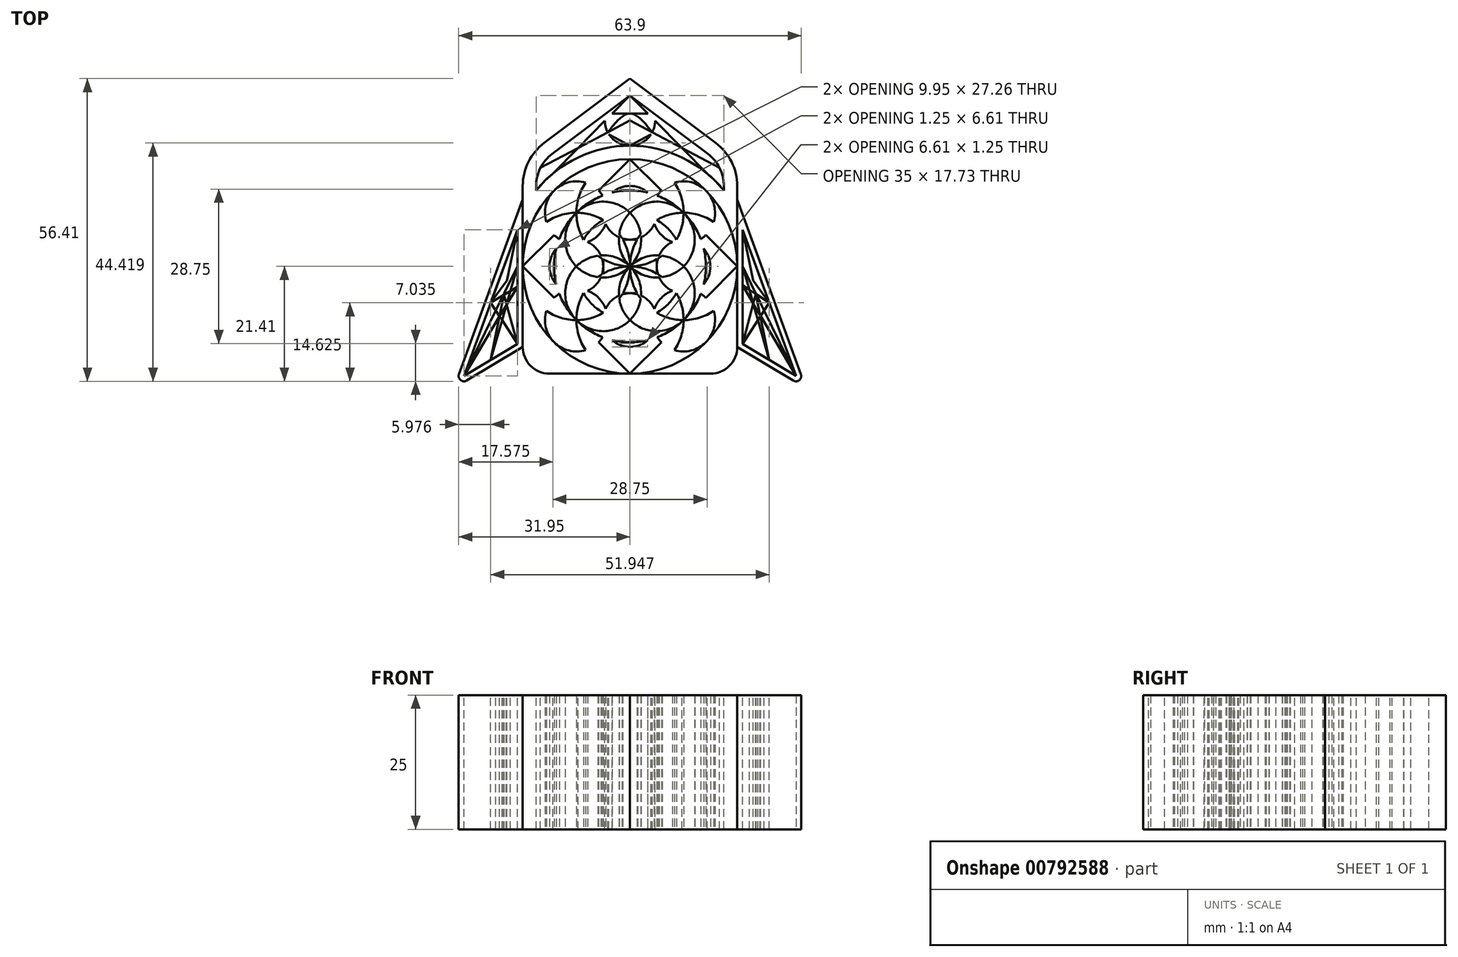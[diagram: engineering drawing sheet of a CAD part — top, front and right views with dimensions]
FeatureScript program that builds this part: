
annotation { "Feature Type Name" : "Feature", "Feature Type Description" : "" }
export const myFeature = defineFeature(function(context is Context, id is Id, definition is map)
    precondition{}
    {
        {
            var Q0;
            Q0=qCreatedBy(makeId("Top.planeOp"),FACE);
            var sketch = newSketch(context, id + "F0", { "sketchPlane" : qUnion([Q0])});
            skLineSegment(sketch, "E0.bottom", {"start": v(-20, 20) * mm, "end": v(20, 20) * mm});
            skLineSegment(sketch, "E0.top", {"start": v(-20, -20) * mm, "end": v(20, -20) * mm});
            skLineSegment(sketch, "E0.left", {"start": v(-20, 20) * mm, "end": v(-20, -20) * mm});
            skLineSegment(sketch, "E0.right", {"start": v(20, 20) * mm, "end": v(20, -20) * mm});
            skPoint(sketch, "E0.middle", {"position": v(0, 0) * mm});
            skCircle(sketch, "E1", {"center": v(0, 0) * mm, "radius": 20 * mm});
            skLineSegment(sketch, "E2", {"start": v(20, 20) * mm, "end": v(-20, -20) * mm, "construction": true});
            skLineSegment(sketch, "E3", {"start": v(-20, 20) * mm, "end": v(0, 35) * mm});
            skLineSegment(sketch, "E4", {"start": v(0, 35) * mm, "end": v(20, 20) * mm});
            skLineSegment(sketch, "E5", {"start": v(0, 35) * mm, "end": v(0, -20) * mm, "construction": true});
            skLineSegment(sketch, "E6", {"start": v(-20, 20) * mm, "end": v(20, -20) * mm, "construction": true});
            skLineSegment(sketch, "E7", {"start": v(0, 20) * mm, "end": v(-10, 20) * mm});
            skLineSegment(sketch, "E8", {"start": v(0, 20) * mm, "end": v(10, 20) * mm});
            skLineSegment(sketch, "E9", {"start": v(20, 20) * mm, "end": v(20, 12.5) * mm});
            skLineSegment(sketch, "E10", {"start": v(20, 12.5) * mm, "end": v(32.86, -22.73) * mm});
            skLineSegment(sketch, "E11", {"start": v(32.86, -22.73) * mm, "end": v(20, -15) * mm});
            skLineSegment(sketch, "E12", {"start": v(20, -15) * mm, "end": v(20, -20) * mm});
            skLineSegment(sketch, "E13", {"start": v(-20, 20) * mm, "end": v(-20, 12.5) * mm});
            skLineSegment(sketch, "E14", {"start": v(-20, 12.5) * mm, "end": v(-32.86, -22.73) * mm});
            skLineSegment(sketch, "E15", {"start": v(-32.86, -22.73) * mm, "end": v(-20, -15) * mm});
            skLineSegment(sketch, "E16", {"start": v(-20, -15) * mm, "end": v(-20, -20) * mm});
            skSolve(sketch);
        }
        {
            var Q0;
            {var subQ3=sQuery(id+"F0.wireOp",EDGE,"E3");Q0=makeQuery(id+"F0.imprint","IMPRINT",FACE,{"disambiguationData":[TD([[makeQuery(id+"F0.imprint","IMPRINT",EDGE,{"derivedFrom":subQ3}),-1.0]])]});}
            var Q1;
            {var subQ3=sQuery(id+"F0.wireOp",EDGE,"E3");Q1=makeQuery(id+"F0.imprint","IMPRINT",FACE,{"disambiguationData":[TD([[makeQuery(id+"F0.imprint","IMPRINT",EDGE,{"derivedFrom":subQ3}),-1.0]])]});}
            var Q2;
            {var subQ3=sQuery(id+"F0.wireOp",EDGE,"0a9cf247-4ca8-4cc3-be67-cc762b10b733");Q2=makeQuery(id+"F0.imprint","IMPRINT",FACE,{"disambiguationData":[TD([[makeQuery(id+"F0.imprint","IMPRINT",EDGE,{"derivedFrom":subQ3}),-1.0]])]});}
            var Q3;
            {var subQ1=sQuery(id+"F0.wireOp",EDGE,"E0.bottom");var subQ6=makeQuery(id+"F0.imprint","IMPRINT",VERTEX,{"disambiguationData":[OD(1.0)],"derivedFrom":subQ1});Q3=makeQuery(id+"F0.imprint","IMPRINT",FACE,{"disambiguationData":[TD([[makeQuery(id+"F0.imprint","IMPRINT",EDGE,{"disambiguationData":[TD([[subQ6,-1.0]])],"derivedFrom":subQ1}),-1.0]])]});}
            var Q4;
            {var subQ1=sQuery(id+"F0.wireOp",EDGE,"E0.bottom");var subQ6=makeQuery(id+"F0.imprint","IMPRINT",VERTEX,{"disambiguationData":[OD(0.0)],"derivedFrom":subQ1});Q4=makeQuery(id+"F0.imprint","IMPRINT",FACE,{"disambiguationData":[TD([[makeQuery(id+"F0.imprint","IMPRINT",EDGE,{"disambiguationData":[TD([[subQ6,1.0]])],"derivedFrom":subQ1}),-1.0]])]});}
            var Q5;
            {var subQ0=sQuery(id+"F0.wireOp",EDGE,"E0.right");var subQ1=sQuery(id+"F0.wireOp",EDGE,"E0.top");var subQ2=makeQuery(id+"F0.imprint","INTERSECT",VERTEX,{"derivedFrom":[subQ1,subQ0]});var subQ7=sQuery(id+"F0.wireOp",EDGE,"E0.left");var subQ8=makeQuery(id+"F0.imprint","INTERSECT",VERTEX,{"derivedFrom":[subQ1,subQ7]});Q5=qUnion([makeQuery(id+"F0.imprint","IMPRINT",FACE,{"disambiguationData":[TD([[makeQuery(id+"F0.imprint","IMPRINT",EDGE,{"disambiguationData":[TD([[subQ8,-1.0]])],"derivedFrom":subQ1}),1.0]])]}),makeQuery(id+"F0.imprint","IMPRINT",FACE,{"disambiguationData":[TD([[makeQuery(id+"F0.imprint","IMPRINT",EDGE,{"disambiguationData":[TD([[subQ2,1.0]])],"derivedFrom":subQ1}),1.0]])]})]);}
            var Q6;
            {var subQ0=sQuery(id+"F0.wireOp",EDGE,"E0.right");var subQ1=sQuery(id+"F0.wireOp",EDGE,"E0.top");var subQ2=makeQuery(id+"F0.imprint","INTERSECT",VERTEX,{"derivedFrom":[subQ1,subQ0]});var subQ7=sQuery(id+"F0.wireOp",EDGE,"E0.left");var subQ8=makeQuery(id+"F0.imprint","INTERSECT",VERTEX,{"derivedFrom":[subQ1,subQ7]});Q6=qUnion([makeQuery(id+"F0.imprint","IMPRINT",FACE,{"disambiguationData":[TD([[makeQuery(id+"F0.imprint","IMPRINT",EDGE,{"disambiguationData":[TD([[subQ8,-1.0]])],"derivedFrom":subQ1}),1.0]])]}),makeQuery(id+"F0.imprint","IMPRINT",FACE,{"disambiguationData":[TD([[makeQuery(id+"F0.imprint","IMPRINT",EDGE,{"disambiguationData":[TD([[subQ2,1.0]])],"derivedFrom":subQ1}),1.0]])]})]);}
            var Q7;
            {var subQ0=sQuery(id+"F0.wireOp",EDGE,"Tc6ELDUx-aZw6-dxSL-uZ0s-LFfPMrrENeSc");Q7=makeQuery(id+"F0.imprint","IMPRINT",FACE,{"disambiguationData":[TD([[makeQuery(id+"F0.imprint","IMPRINT",EDGE,{"derivedFrom":subQ0}),-1.0]])]});}
            var Q8;
            {var subQ0=sQuery(id+"F0.wireOp",EDGE,"qauVQVhD-89ha-aMvt-0F9t-eZ8ksP4P0BOe");Q8=makeQuery(id+"F0.imprint","IMPRINT",FACE,{"disambiguationData":[TD([[makeQuery(id+"F0.imprint","IMPRINT",EDGE,{"derivedFrom":subQ0}),-1.0]])]});}
            var Q9;
            {var subQ3=sQuery(id+"F0.wireOp",EDGE,"E3");Q9=makeQuery(id+"F0.imprint","IMPRINT",FACE,{"disambiguationData":[TD([[makeQuery(id+"F0.imprint","IMPRINT",EDGE,{"derivedFrom":subQ3}),-1.0]])]});}
            extrude(context, id + "F1", {"entities" : qUnion([Q0, Q1, Q2, Q3, Q4, Q5, Q6, Q7, Q8, Q9]), "endBound" : BoundingType.SYMMETRIC, "depth" : 25 * mm, "offsetDistance" : 25 * mm});
        }
        {
            var Q0;
            Q0=makeQuery(id+"F1.opExtrude","SWEPT_EDGE",EDGE,{"disambiguationData":[OSD([sQuery(id+"F0.wireOp",EDGE,"E0.bottom"),sQuery(id+"F0.wireOp",EDGE,"E0.left"),sQuery(id+"F0.wireOp",EDGE,"E3")])]});
            var Q1;
            Q1=makeQuery(id+"F1.opExtrude","SWEPT_EDGE",EDGE,{"disambiguationData":[OSD([sQuery(id+"F0.wireOp",EDGE,"E0.bottom"),sQuery(id+"F0.wireOp",EDGE,"E0.right"),sQuery(id+"F0.wireOp",EDGE,"E4")])]});
            fillet(context, id + "F2", {"entities" : qUnion([Q0, Q1]), "radius" : 10 * mm, "tangentPropagation" : true, "allowEdgeOverflow" : false});
        }
        {
            var Q0;
            Q0=makeQuery(id+"F1.opExtrude","CAP_FACE",FACE,{"disambiguationData":[OSD([sQuery(id+"F0.wireOp",EDGE,"E0.left"),sQuery(id+"F0.wireOp",EDGE,"E0.right"),sQuery(id+"F0.wireOp",EDGE,"E1"),sQuery(id+"F0.wireOp",EDGE,"E3"),sQuery(id+"F0.wireOp",EDGE,"E4")])],"isStart":false});
            var Q1;
            Q1=makeQuery(id+"F1.opExtrude","CAP_FACE",FACE,{"disambiguationData":[OSD([sQuery(id+"F0.wireOp",EDGE,"E0.left"),sQuery(id+"F0.wireOp",EDGE,"E0.right"),sQuery(id+"F0.wireOp",EDGE,"E1"),sQuery(id+"F0.wireOp",EDGE,"E3"),sQuery(id+"F0.wireOp",EDGE,"E4")])],"isStart":true});
            shell(context, id + "F3", {"entities" : qUnion([Q0, Q1]), "thickness" : 2.5 * mm});
        }
        {
            var Q0;
            Q0=qCreatedBy(makeId("Top.planeOp"),FACE);
            var sketch = newSketch(context, id + "F4", { "sketchPlane" : qUnion([Q0])});
            skCircle(sketch, "E17", {"center": v(0, 0) * mm, "radius": 20 * mm});
            skLineSegment(sketch, "E18", {"start": v(0, 0) * mm, "end": v(0, 20) * mm});
            skLineSegment(sketch, "E19", {"start": v(0, 0) * mm, "end": v(0, -20) * mm});
            skLineSegment(sketch, "E20", {"start": v(0, 0) * mm, "end": v(20, 0) * mm});
            skLineSegment(sketch, "E21", {"start": v(0, 0) * mm, "end": v(-20, 0) * mm});
            skLineSegment(sketch, "E22", {"start": v(0, 20) * mm, "end": v(-20, 0) * mm});
            skLineSegment(sketch, "E23", {"start": v(-20, 0) * mm, "end": v(0, -20) * mm});
            skLineSegment(sketch, "E24", {"start": v(0, -20) * mm, "end": v(20, 0) * mm});
            skLineSegment(sketch, "E25", {"start": v(20, 0) * mm, "end": v(0, 20) * mm});
            skLineSegment(sketch, "E26", {"start": v(0, 0) * mm, "end": v(-10, 10) * mm});
            skLineSegment(sketch, "E27", {"start": v(0, 0) * mm, "end": v(10, -10) * mm});
            skLineSegment(sketch, "E28", {"start": v(0, 0) * mm, "end": v(10, 10) * mm});
            skLineSegment(sketch, "E29", {"start": v(0, 0) * mm, "end": v(-10, -10) * mm});
            skCircle(sketch, "E30", {"center": v(-5, 5) * mm, "radius": 7.07 * mm});
            skCircle(sketch, "E31", {"center": v(5, 5) * mm, "radius": 7.07 * mm});
            skCircle(sketch, "E32", {"center": v(5, -5) * mm, "radius": 7.07 * mm});
            skCircle(sketch, "E33", {"center": v(-5, -5) * mm, "radius": 7.07 * mm});
            skCircle(sketch, "E34", {"center": v(0, -10) * mm, "radius": 10 * mm});
            skCircle(sketch, "E35", {"center": v(10, 0) * mm, "radius": 10 * mm});
            skCircle(sketch, "E36", {"center": v(0, 10) * mm, "radius": 10 * mm});
            skCircle(sketch, "E37", {"center": v(-10, 0) * mm, "radius": 10 * mm});
            skLineSegment(sketch, "E38", {"start": v(5, 5) * mm, "end": v(5, -5) * mm});
            skLineSegment(sketch, "E39", {"start": v(-5, -5) * mm, "end": v(5, -5) * mm});
            skLineSegment(sketch, "E40", {"start": v(-5, -5) * mm, "end": v(-5, 5) * mm});
            skLineSegment(sketch, "E41", {"start": v(-5, 5) * mm, "end": v(5, 5) * mm});
            skLineSegment(sketch, "E42", {"start": v(-10, 10) * mm, "end": v(10, 10) * mm});
            skLineSegment(sketch, "E43", {"start": v(10, 10) * mm, "end": v(10, -10) * mm});
            skLineSegment(sketch, "E44", {"start": v(10, -10) * mm, "end": v(-10, -10) * mm});
            skLineSegment(sketch, "E45", {"start": v(-10, -10) * mm, "end": v(-10, 10) * mm});
            skCircle(sketch, "E46", {"center": v(-10, -10) * mm, "radius": 5.86 * mm});
            skCircle(sketch, "E47", {"center": v(10, -10) * mm, "radius": 5.86 * mm});
            skCircle(sketch, "E48", {"center": v(10, 10) * mm, "radius": 5.86 * mm});
            skCircle(sketch, "E49", {"center": v(-10, 10) * mm, "radius": 5.86 * mm});
            skCircle(sketch, "E50", {"center": v(0, 0) * mm, "radius": 10 * mm});
            skCircle(sketch, "E51", {"center": v(0, 0) * mm, "radius": 14.14 * mm});
            skCircle(sketch, "E52", {"center": v(10, 0) * mm, "radius": 5 * mm});
            skCircle(sketch, "E53", {"center": v(0, -10) * mm, "radius": 5 * mm});
            skCircle(sketch, "E54", {"center": v(-10, 0) * mm, "radius": 5 * mm});
            skCircle(sketch, "E55", {"center": v(0, 10) * mm, "radius": 5 * mm});
            skSolve(sketch);
        }
        {
            var Q0;
            {var subQ0=sQuery(id+"F4.wireOp",EDGE,"E37");var subQ3=sQuery(id+"F4.wireOp",EDGE,"E41");var subQ5=makeQuery(id+"F4.imprint","INTERSECT",VERTEX,{"derivedFrom":[subQ0,subQ3]});Q0=makeQuery(id+"F4.imprint","IMPRINT",FACE,{"disambiguationData":[TD([[makeQuery(id+"F4.imprint","IMPRINT",EDGE,{"disambiguationData":[TD([[subQ5,-1.0]])],"derivedFrom":subQ3}),-1.0]])]});}
            var Q1;
            {var subQ0=sQuery(id+"F4.wireOp",EDGE,"E35");var subQ3=sQuery(id+"F4.wireOp",EDGE,"E41");var subQ5=makeQuery(id+"F4.imprint","INTERSECT",VERTEX,{"derivedFrom":[subQ0,subQ3]});Q1=makeQuery(id+"F4.imprint","IMPRINT",FACE,{"disambiguationData":[TD([[makeQuery(id+"F4.imprint","IMPRINT",EDGE,{"disambiguationData":[TD([[subQ5,1.0]])],"derivedFrom":subQ3}),-1.0]])]});}
            var Q2;
            {var subQ0=sQuery(id+"F4.wireOp",EDGE,"E36");var subQ3=sQuery(id+"F4.wireOp",EDGE,"E38");var subQ5=makeQuery(id+"F4.imprint","INTERSECT",VERTEX,{"derivedFrom":[subQ0,subQ3]});Q2=makeQuery(id+"F4.imprint","IMPRINT",FACE,{"disambiguationData":[TD([[makeQuery(id+"F4.imprint","IMPRINT",EDGE,{"disambiguationData":[TD([[subQ5,-1.0]])],"derivedFrom":subQ3}),-1.0]])]});}
            var Q3;
            {var subQ0=sQuery(id+"F4.wireOp",EDGE,"E34");var subQ3=sQuery(id+"F4.wireOp",EDGE,"E38");var subQ5=makeQuery(id+"F4.imprint","INTERSECT",VERTEX,{"derivedFrom":[subQ0,subQ3]});Q3=makeQuery(id+"F4.imprint","IMPRINT",FACE,{"disambiguationData":[TD([[makeQuery(id+"F4.imprint","IMPRINT",EDGE,{"disambiguationData":[TD([[subQ5,1.0]])],"derivedFrom":subQ3}),-1.0]])]});}
            var Q4;
            {var subQ0=sQuery(id+"F4.wireOp",EDGE,"E35");var subQ3=sQuery(id+"F4.wireOp",EDGE,"E39");var subQ5=makeQuery(id+"F4.imprint","INTERSECT",VERTEX,{"derivedFrom":[subQ0,subQ3]});Q4=makeQuery(id+"F4.imprint","IMPRINT",FACE,{"disambiguationData":[TD([[makeQuery(id+"F4.imprint","IMPRINT",EDGE,{"disambiguationData":[TD([[subQ5,1.0]])],"derivedFrom":subQ3}),1.0]])]});}
            var Q5;
            {var subQ0=sQuery(id+"F4.wireOp",EDGE,"E37");var subQ3=sQuery(id+"F4.wireOp",EDGE,"E39");var subQ5=makeQuery(id+"F4.imprint","INTERSECT",VERTEX,{"derivedFrom":[subQ0,subQ3]});Q5=makeQuery(id+"F4.imprint","IMPRINT",FACE,{"disambiguationData":[TD([[makeQuery(id+"F4.imprint","IMPRINT",EDGE,{"disambiguationData":[TD([[subQ5,-1.0]])],"derivedFrom":subQ3}),1.0]])]});}
            var Q6;
            {var subQ0=sQuery(id+"F4.wireOp",EDGE,"E34");var subQ3=sQuery(id+"F4.wireOp",EDGE,"E40");var subQ5=makeQuery(id+"F4.imprint","INTERSECT",VERTEX,{"derivedFrom":[subQ0,subQ3]});Q6=makeQuery(id+"F4.imprint","IMPRINT",FACE,{"disambiguationData":[TD([[makeQuery(id+"F4.imprint","IMPRINT",EDGE,{"disambiguationData":[TD([[subQ5,-1.0]])],"derivedFrom":subQ3}),-1.0]])]});}
            var Q7;
            {var subQ0=sQuery(id+"F4.wireOp",EDGE,"E36");var subQ3=sQuery(id+"F4.wireOp",EDGE,"E40");var subQ5=makeQuery(id+"F4.imprint","INTERSECT",VERTEX,{"derivedFrom":[subQ0,subQ3]});Q7=makeQuery(id+"F4.imprint","IMPRINT",FACE,{"disambiguationData":[TD([[makeQuery(id+"F4.imprint","IMPRINT",EDGE,{"disambiguationData":[TD([[subQ5,1.0]])],"derivedFrom":subQ3}),-1.0]])]});}
            var Q8;
            {var subQ3=sQuery(id+"F4.wireOp",EDGE,"E33");var subQ5=sQuery(id+"F4.wireOp",EDGE,"E36");var subQ6=makeQuery(id+"F4.imprint","INTERSECT",VERTEX,{"derivedFrom":[subQ3,subQ5]});Q8=makeQuery(id+"F4.imprint","IMPRINT",FACE,{"disambiguationData":[TD([[makeQuery(id+"F4.imprint","IMPRINT",EDGE,{"disambiguationData":[TD([[subQ6,-1.0]])],"derivedFrom":subQ5}),-1.0]])]});}
            var Q9;
            {var subQ3=sQuery(id+"F4.wireOp",EDGE,"E30");var subQ5=sQuery(id+"F4.wireOp",EDGE,"E34");var subQ6=makeQuery(id+"F4.imprint","INTERSECT",VERTEX,{"derivedFrom":[subQ3,subQ5]});Q9=makeQuery(id+"F4.imprint","IMPRINT",FACE,{"disambiguationData":[TD([[makeQuery(id+"F4.imprint","IMPRINT",EDGE,{"disambiguationData":[TD([[subQ6,1.0]])],"derivedFrom":subQ5}),-1.0]])]});}
            var Q10;
            {var subQ3=sQuery(id+"F4.wireOp",EDGE,"E32");var subQ5=sQuery(id+"F4.wireOp",EDGE,"E37");var subQ6=makeQuery(id+"F4.imprint","INTERSECT",VERTEX,{"derivedFrom":[subQ3,subQ5]});Q10=makeQuery(id+"F4.imprint","IMPRINT",FACE,{"disambiguationData":[TD([[makeQuery(id+"F4.imprint","IMPRINT",EDGE,{"disambiguationData":[TD([[subQ6,-1.0]])],"derivedFrom":subQ5}),-1.0]])]});}
            var Q11;
            {var subQ3=sQuery(id+"F4.wireOp",EDGE,"E33");var subQ5=sQuery(id+"F4.wireOp",EDGE,"E35");var subQ6=makeQuery(id+"F4.imprint","INTERSECT",VERTEX,{"derivedFrom":[subQ3,subQ5]});Q11=makeQuery(id+"F4.imprint","IMPRINT",FACE,{"disambiguationData":[TD([[makeQuery(id+"F4.imprint","IMPRINT",EDGE,{"disambiguationData":[TD([[subQ6,1.0]])],"derivedFrom":subQ5}),-1.0]])]});}
            var Q12;
            {var subQ3=sQuery(id+"F4.wireOp",EDGE,"E31");var subQ5=sQuery(id+"F4.wireOp",EDGE,"E34");var subQ6=makeQuery(id+"F4.imprint","INTERSECT",VERTEX,{"derivedFrom":[subQ3,subQ5]});Q12=makeQuery(id+"F4.imprint","IMPRINT",FACE,{"disambiguationData":[TD([[makeQuery(id+"F4.imprint","IMPRINT",EDGE,{"disambiguationData":[TD([[subQ6,-1.0]])],"derivedFrom":subQ5}),-1.0]])]});}
            var Q13;
            {var subQ3=sQuery(id+"F4.wireOp",EDGE,"E32");var subQ5=sQuery(id+"F4.wireOp",EDGE,"E36");var subQ6=makeQuery(id+"F4.imprint","INTERSECT",VERTEX,{"derivedFrom":[subQ3,subQ5]});Q13=makeQuery(id+"F4.imprint","IMPRINT",FACE,{"disambiguationData":[TD([[makeQuery(id+"F4.imprint","IMPRINT",EDGE,{"disambiguationData":[TD([[subQ6,1.0]])],"derivedFrom":subQ5}),-1.0]])]});}
            var Q14;
            {var subQ3=sQuery(id+"F4.wireOp",EDGE,"E31");var subQ5=sQuery(id+"F4.wireOp",EDGE,"E37");var subQ6=makeQuery(id+"F4.imprint","INTERSECT",VERTEX,{"derivedFrom":[subQ3,subQ5]});Q14=makeQuery(id+"F4.imprint","IMPRINT",FACE,{"disambiguationData":[TD([[makeQuery(id+"F4.imprint","IMPRINT",EDGE,{"disambiguationData":[TD([[subQ6,1.0]])],"derivedFrom":subQ5}),-1.0]])]});}
            var Q15;
            {var subQ3=sQuery(id+"F4.wireOp",EDGE,"E30");var subQ5=sQuery(id+"F4.wireOp",EDGE,"E35");var subQ6=makeQuery(id+"F4.imprint","INTERSECT",VERTEX,{"derivedFrom":[subQ3,subQ5]});Q15=makeQuery(id+"F4.imprint","IMPRINT",FACE,{"disambiguationData":[TD([[makeQuery(id+"F4.imprint","IMPRINT",EDGE,{"disambiguationData":[TD([[subQ6,-1.0]])],"derivedFrom":subQ5}),-1.0]])]});}
            var Q16;
            {var subQ0=sQuery(id+"F4.wireOp",EDGE,"E46");var subQ1=sQuery(id+"F4.wireOp",EDGE,"E33");var subQ2=makeQuery(id+"F4.imprint","INTERSECT",VERTEX,{"disambiguationData":[OD(0.0)],"derivedFrom":[subQ1,subQ0]});Q16=makeQuery(id+"F4.imprint","IMPRINT",FACE,{"disambiguationData":[TD([[makeQuery(id+"F4.imprint","IMPRINT",EDGE,{"disambiguationData":[TD([[subQ2,-1.0]])],"derivedFrom":subQ0}),-1.0]])]});}
            var Q17;
            {var subQ5=sQuery(id+"F4.wireOp",EDGE,"E49");var subQ6=sQuery(id+"F4.wireOp",EDGE,"E30");var subQ7=makeQuery(id+"F4.imprint","INTERSECT",VERTEX,{"disambiguationData":[OD(1.0)],"derivedFrom":[subQ6,subQ5]});Q17=makeQuery(id+"F4.imprint","IMPRINT",FACE,{"disambiguationData":[TD([[makeQuery(id+"F4.imprint","IMPRINT",EDGE,{"disambiguationData":[TD([[subQ7,1.0]])],"derivedFrom":subQ5}),-1.0]])]});}
            var Q18;
            {var subQ0=sQuery(id+"F4.wireOp",EDGE,"E51");var subQ1=sQuery(id+"F4.wireOp",EDGE,"E49");var subQ2=makeQuery(id+"F4.imprint","INTERSECT",VERTEX,{"disambiguationData":[OD(1.0)],"derivedFrom":[subQ1,subQ0]});Q18=makeQuery(id+"F4.imprint","IMPRINT",FACE,{"disambiguationData":[TD([[makeQuery(id+"F4.imprint","IMPRINT",EDGE,{"disambiguationData":[TD([[subQ2,-1.0]])],"derivedFrom":subQ1}),-1.0]])]});}
            var Q19;
            {var subQ0=sQuery(id+"F4.wireOp",EDGE,"E51");var subQ5=sQuery(id+"F4.wireOp",EDGE,"E49");var subQ6=makeQuery(id+"F4.imprint","INTERSECT",VERTEX,{"disambiguationData":[OD(1.0)],"derivedFrom":[subQ5,subQ0]});Q19=makeQuery(id+"F4.imprint","IMPRINT",FACE,{"disambiguationData":[TD([[makeQuery(id+"F4.imprint","IMPRINT",EDGE,{"disambiguationData":[TD([[subQ6,-1.0]])],"derivedFrom":subQ5}),1.0]])]});}
            var Q20;
            {var subQ0=sQuery(id+"F4.wireOp",EDGE,"E54");var subQ1=sQuery(id+"F4.wireOp",EDGE,"E46");var subQ2=makeQuery(id+"F4.imprint","INTERSECT",VERTEX,{"disambiguationData":[OD(1.0)],"derivedFrom":[subQ1,subQ0]});Q20=makeQuery(id+"F4.imprint","IMPRINT",FACE,{"disambiguationData":[TD([[makeQuery(id+"F4.imprint","IMPRINT",EDGE,{"disambiguationData":[TD([[subQ2,-1.0]])],"derivedFrom":subQ1}),-1.0]])]});}
            var Q21;
            {var subQ3=sQuery(id+"F4.wireOp",EDGE,"E54");var subQ5=sQuery(id+"F4.wireOp",EDGE,"E46");var subQ6=makeQuery(id+"F4.imprint","INTERSECT",VERTEX,{"disambiguationData":[OD(1.0)],"derivedFrom":[subQ5,subQ3]});Q21=makeQuery(id+"F4.imprint","IMPRINT",FACE,{"disambiguationData":[TD([[makeQuery(id+"F4.imprint","IMPRINT",EDGE,{"disambiguationData":[TD([[subQ6,-1.0]])],"derivedFrom":subQ5}),1.0]])]});}
            var Q22;
            {var subQ0=sQuery(id+"F4.wireOp",EDGE,"E46");var subQ1=sQuery(id+"F4.wireOp",EDGE,"E33");var subQ2=makeQuery(id+"F4.imprint","INTERSECT",VERTEX,{"disambiguationData":[OD(1.0)],"derivedFrom":[subQ1,subQ0]});Q22=makeQuery(id+"F4.imprint","IMPRINT",FACE,{"disambiguationData":[TD([[makeQuery(id+"F4.imprint","IMPRINT",EDGE,{"disambiguationData":[TD([[subQ2,1.0]])],"derivedFrom":subQ0}),-1.0]])]});}
            var Q23;
            {var subQ5=sQuery(id+"F4.wireOp",EDGE,"E47");var subQ6=sQuery(id+"F4.wireOp",EDGE,"E32");var subQ7=makeQuery(id+"F4.imprint","INTERSECT",VERTEX,{"disambiguationData":[OD(1.0)],"derivedFrom":[subQ6,subQ5]});Q23=makeQuery(id+"F4.imprint","IMPRINT",FACE,{"disambiguationData":[TD([[makeQuery(id+"F4.imprint","IMPRINT",EDGE,{"disambiguationData":[TD([[subQ7,-1.0]])],"derivedFrom":subQ5}),-1.0]])]});}
            var Q24;
            {var subQ0=sQuery(id+"F4.wireOp",EDGE,"E53");var subQ1=sQuery(id+"F4.wireOp",EDGE,"E47");var subQ2=makeQuery(id+"F4.imprint","INTERSECT",VERTEX,{"disambiguationData":[OD(1.0)],"derivedFrom":[subQ1,subQ0]});Q24=makeQuery(id+"F4.imprint","IMPRINT",FACE,{"disambiguationData":[TD([[makeQuery(id+"F4.imprint","IMPRINT",EDGE,{"disambiguationData":[TD([[subQ2,-1.0]])],"derivedFrom":subQ1}),-1.0]])]});}
            var Q25;
            {var subQ3=sQuery(id+"F4.wireOp",EDGE,"E53");var subQ5=sQuery(id+"F4.wireOp",EDGE,"E47");var subQ6=makeQuery(id+"F4.imprint","INTERSECT",VERTEX,{"disambiguationData":[OD(1.0)],"derivedFrom":[subQ5,subQ3]});Q25=makeQuery(id+"F4.imprint","IMPRINT",FACE,{"disambiguationData":[TD([[makeQuery(id+"F4.imprint","IMPRINT",EDGE,{"disambiguationData":[TD([[subQ6,-1.0]])],"derivedFrom":subQ5}),1.0]])]});}
            var Q26;
            {var subQ0=sQuery(id+"F4.wireOp",EDGE,"E51");var subQ1=sQuery(id+"F4.wireOp",EDGE,"E46");var subQ2=makeQuery(id+"F4.imprint","INTERSECT",VERTEX,{"disambiguationData":[OD(1.0)],"derivedFrom":[subQ1,subQ0]});Q26=makeQuery(id+"F4.imprint","IMPRINT",FACE,{"disambiguationData":[TD([[makeQuery(id+"F4.imprint","IMPRINT",EDGE,{"disambiguationData":[TD([[subQ2,-1.0]])],"derivedFrom":subQ1}),-1.0]])]});}
            var Q27;
            {var subQ0=sQuery(id+"F4.wireOp",EDGE,"E51");var subQ5=sQuery(id+"F4.wireOp",EDGE,"E46");var subQ7=makeQuery(id+"F4.imprint","INTERSECT",VERTEX,{"disambiguationData":[OD(1.0)],"derivedFrom":[subQ5,subQ0]});Q27=makeQuery(id+"F4.imprint","IMPRINT",FACE,{"disambiguationData":[TD([[makeQuery(id+"F4.imprint","IMPRINT",EDGE,{"disambiguationData":[TD([[subQ7,-1.0]])],"derivedFrom":subQ5}),1.0]])]});}
            var Q28;
            {var subQ5=sQuery(id+"F4.wireOp",EDGE,"E47");var subQ6=sQuery(id+"F4.wireOp",EDGE,"E32");var subQ7=makeQuery(id+"F4.imprint","INTERSECT",VERTEX,{"disambiguationData":[OD(0.0)],"derivedFrom":[subQ6,subQ5]});Q28=makeQuery(id+"F4.imprint","IMPRINT",FACE,{"disambiguationData":[TD([[makeQuery(id+"F4.imprint","IMPRINT",EDGE,{"disambiguationData":[TD([[subQ7,1.0]])],"derivedFrom":subQ5}),-1.0]])]});}
            var Q29;
            {var subQ0=sQuery(id+"F4.wireOp",EDGE,"E51");var subQ1=sQuery(id+"F4.wireOp",EDGE,"E47");var subQ2=makeQuery(id+"F4.imprint","INTERSECT",VERTEX,{"disambiguationData":[OD(0.0)],"derivedFrom":[subQ1,subQ0]});Q29=makeQuery(id+"F4.imprint","IMPRINT",FACE,{"disambiguationData":[TD([[makeQuery(id+"F4.imprint","IMPRINT",EDGE,{"disambiguationData":[TD([[subQ2,-1.0]])],"derivedFrom":subQ1}),-1.0]])]});}
            var Q30;
            {var subQ0=sQuery(id+"F4.wireOp",EDGE,"E51");var subQ5=sQuery(id+"F4.wireOp",EDGE,"E47");var subQ6=makeQuery(id+"F4.imprint","INTERSECT",VERTEX,{"disambiguationData":[OD(0.0)],"derivedFrom":[subQ5,subQ0]});Q30=makeQuery(id+"F4.imprint","IMPRINT",FACE,{"disambiguationData":[TD([[makeQuery(id+"F4.imprint","IMPRINT",EDGE,{"disambiguationData":[TD([[subQ6,-1.0]])],"derivedFrom":subQ5}),1.0]])]});}
            var Q31;
            {var subQ5=sQuery(id+"F4.wireOp",EDGE,"E48");var subQ6=sQuery(id+"F4.wireOp",EDGE,"E31");var subQ7=makeQuery(id+"F4.imprint","INTERSECT",VERTEX,{"disambiguationData":[OD(1.0)],"derivedFrom":[subQ6,subQ5]});Q31=makeQuery(id+"F4.imprint","IMPRINT",FACE,{"disambiguationData":[TD([[makeQuery(id+"F4.imprint","IMPRINT",EDGE,{"disambiguationData":[TD([[subQ7,-1.0]])],"derivedFrom":subQ5}),-1.0]])]});}
            var Q32;
            {var subQ0=sQuery(id+"F4.wireOp",EDGE,"E52");var subQ1=sQuery(id+"F4.wireOp",EDGE,"E48");var subQ2=makeQuery(id+"F4.imprint","INTERSECT",VERTEX,{"disambiguationData":[OD(1.0)],"derivedFrom":[subQ1,subQ0]});Q32=makeQuery(id+"F4.imprint","IMPRINT",FACE,{"disambiguationData":[TD([[makeQuery(id+"F4.imprint","IMPRINT",EDGE,{"disambiguationData":[TD([[subQ2,-1.0]])],"derivedFrom":subQ1}),-1.0]])]});}
            var Q33;
            {var subQ3=sQuery(id+"F4.wireOp",EDGE,"E52");var subQ5=sQuery(id+"F4.wireOp",EDGE,"E48");var subQ6=makeQuery(id+"F4.imprint","INTERSECT",VERTEX,{"disambiguationData":[OD(1.0)],"derivedFrom":[subQ5,subQ3]});Q33=makeQuery(id+"F4.imprint","IMPRINT",FACE,{"disambiguationData":[TD([[makeQuery(id+"F4.imprint","IMPRINT",EDGE,{"disambiguationData":[TD([[subQ6,-1.0]])],"derivedFrom":subQ5}),1.0]])]});}
            var Q34;
            {var subQ5=sQuery(id+"F4.wireOp",EDGE,"E48");var subQ6=sQuery(id+"F4.wireOp",EDGE,"E31");var subQ7=makeQuery(id+"F4.imprint","INTERSECT",VERTEX,{"disambiguationData":[OD(0.0)],"derivedFrom":[subQ6,subQ5]});Q34=makeQuery(id+"F4.imprint","IMPRINT",FACE,{"disambiguationData":[TD([[makeQuery(id+"F4.imprint","IMPRINT",EDGE,{"disambiguationData":[TD([[subQ7,1.0]])],"derivedFrom":subQ5}),-1.0]])]});}
            var Q35;
            {var subQ5=sQuery(id+"F4.wireOp",EDGE,"E49");var subQ6=sQuery(id+"F4.wireOp",EDGE,"E30");var subQ7=makeQuery(id+"F4.imprint","INTERSECT",VERTEX,{"disambiguationData":[OD(0.0)],"derivedFrom":[subQ6,subQ5]});Q35=makeQuery(id+"F4.imprint","IMPRINT",FACE,{"disambiguationData":[TD([[makeQuery(id+"F4.imprint","IMPRINT",EDGE,{"disambiguationData":[TD([[subQ7,-1.0]])],"derivedFrom":subQ5}),-1.0]])]});}
            var Q36;
            {var subQ0=sQuery(id+"F4.wireOp",EDGE,"E55");var subQ1=sQuery(id+"F4.wireOp",EDGE,"E49");var subQ2=makeQuery(id+"F4.imprint","INTERSECT",VERTEX,{"disambiguationData":[OD(0.0)],"derivedFrom":[subQ1,subQ0]});Q36=makeQuery(id+"F4.imprint","IMPRINT",FACE,{"disambiguationData":[TD([[makeQuery(id+"F4.imprint","IMPRINT",EDGE,{"disambiguationData":[TD([[subQ2,-1.0]])],"derivedFrom":subQ1}),-1.0]])]});}
            var Q37;
            {var subQ3=sQuery(id+"F4.wireOp",EDGE,"E55");var subQ5=sQuery(id+"F4.wireOp",EDGE,"E49");var subQ6=makeQuery(id+"F4.imprint","INTERSECT",VERTEX,{"disambiguationData":[OD(0.0)],"derivedFrom":[subQ5,subQ3]});Q37=makeQuery(id+"F4.imprint","IMPRINT",FACE,{"disambiguationData":[TD([[makeQuery(id+"F4.imprint","IMPRINT",EDGE,{"disambiguationData":[TD([[subQ6,-1.0]])],"derivedFrom":subQ5}),1.0]])]});}
            var Q38;
            {var subQ0=sQuery(id+"F4.wireOp",EDGE,"E51");var subQ1=sQuery(id+"F4.wireOp",EDGE,"E48");var subQ2=makeQuery(id+"F4.imprint","INTERSECT",VERTEX,{"disambiguationData":[OD(0.0)],"derivedFrom":[subQ1,subQ0]});Q38=makeQuery(id+"F4.imprint","IMPRINT",FACE,{"disambiguationData":[TD([[makeQuery(id+"F4.imprint","IMPRINT",EDGE,{"disambiguationData":[TD([[subQ2,-1.0]])],"derivedFrom":subQ1}),-1.0]])]});}
            var Q39;
            {var subQ0=sQuery(id+"F4.wireOp",EDGE,"E51");var subQ5=sQuery(id+"F4.wireOp",EDGE,"E48");var subQ6=makeQuery(id+"F4.imprint","INTERSECT",VERTEX,{"disambiguationData":[OD(0.0)],"derivedFrom":[subQ5,subQ0]});Q39=makeQuery(id+"F4.imprint","IMPRINT",FACE,{"disambiguationData":[TD([[makeQuery(id+"F4.imprint","IMPRINT",EDGE,{"disambiguationData":[TD([[subQ6,-1.0]])],"derivedFrom":subQ5}),1.0]])]});}
            var Q40;
            {var subQ1=sQuery(id+"F4.wireOp",EDGE,"E27");var subQ3=sQuery(id+"F4.wireOp",EDGE,"E50");var subQ4=makeQuery(id+"F4.imprint","INTERSECT",VERTEX,{"derivedFrom":[subQ1,subQ3]});Q40=makeQuery(id+"F4.imprint","IMPRINT",FACE,{"disambiguationData":[TD([[makeQuery(id+"F4.imprint","IMPRINT",EDGE,{"disambiguationData":[TD([[subQ4,1.0]])],"derivedFrom":subQ3}),-1.0]])]});}
            var Q41;
            {var subQ1=sQuery(id+"F4.wireOp",EDGE,"E27");var subQ3=sQuery(id+"F4.wireOp",EDGE,"E50");var subQ4=makeQuery(id+"F4.imprint","INTERSECT",VERTEX,{"derivedFrom":[subQ1,subQ3]});Q41=makeQuery(id+"F4.imprint","IMPRINT",FACE,{"disambiguationData":[TD([[makeQuery(id+"F4.imprint","IMPRINT",EDGE,{"disambiguationData":[TD([[subQ4,-1.0]])],"derivedFrom":subQ3}),-1.0]])]});}
            var Q42;
            {var subQ1=sQuery(id+"F4.wireOp",EDGE,"E29");var subQ3=sQuery(id+"F4.wireOp",EDGE,"E50");var subQ4=makeQuery(id+"F4.imprint","INTERSECT",VERTEX,{"derivedFrom":[subQ1,subQ3]});Q42=makeQuery(id+"F4.imprint","IMPRINT",FACE,{"disambiguationData":[TD([[makeQuery(id+"F4.imprint","IMPRINT",EDGE,{"disambiguationData":[TD([[subQ4,-1.0]])],"derivedFrom":subQ3}),-1.0]])]});}
            var Q43;
            {var subQ1=sQuery(id+"F4.wireOp",EDGE,"E29");var subQ3=sQuery(id+"F4.wireOp",EDGE,"E50");var subQ4=makeQuery(id+"F4.imprint","INTERSECT",VERTEX,{"derivedFrom":[subQ1,subQ3]});Q43=makeQuery(id+"F4.imprint","IMPRINT",FACE,{"disambiguationData":[TD([[makeQuery(id+"F4.imprint","IMPRINT",EDGE,{"disambiguationData":[TD([[subQ4,1.0]])],"derivedFrom":subQ3}),-1.0]])]});}
            var Q44;
            {var subQ1=sQuery(id+"F4.wireOp",EDGE,"E26");var subQ3=sQuery(id+"F4.wireOp",EDGE,"E50");var subQ4=makeQuery(id+"F4.imprint","INTERSECT",VERTEX,{"derivedFrom":[subQ1,subQ3]});Q44=makeQuery(id+"F4.imprint","IMPRINT",FACE,{"disambiguationData":[TD([[makeQuery(id+"F4.imprint","IMPRINT",EDGE,{"disambiguationData":[TD([[subQ4,-1.0]])],"derivedFrom":subQ3}),-1.0]])]});}
            var Q45;
            {var subQ1=sQuery(id+"F4.wireOp",EDGE,"E26");var subQ3=sQuery(id+"F4.wireOp",EDGE,"E50");var subQ4=makeQuery(id+"F4.imprint","INTERSECT",VERTEX,{"derivedFrom":[subQ1,subQ3]});Q45=makeQuery(id+"F4.imprint","IMPRINT",FACE,{"disambiguationData":[TD([[makeQuery(id+"F4.imprint","IMPRINT",EDGE,{"disambiguationData":[TD([[subQ4,1.0]])],"derivedFrom":subQ3}),-1.0]])]});}
            var Q46;
            {var subQ1=sQuery(id+"F4.wireOp",EDGE,"E28");var subQ3=sQuery(id+"F4.wireOp",EDGE,"E50");var subQ4=makeQuery(id+"F4.imprint","INTERSECT",VERTEX,{"derivedFrom":[subQ1,subQ3]});Q46=makeQuery(id+"F4.imprint","IMPRINT",FACE,{"disambiguationData":[TD([[makeQuery(id+"F4.imprint","IMPRINT",EDGE,{"disambiguationData":[TD([[subQ4,-1.0]])],"derivedFrom":subQ3}),-1.0]])]});}
            var Q47;
            {var subQ1=sQuery(id+"F4.wireOp",EDGE,"E28");var subQ3=sQuery(id+"F4.wireOp",EDGE,"E50");var subQ4=makeQuery(id+"F4.imprint","INTERSECT",VERTEX,{"derivedFrom":[subQ1,subQ3]});Q47=makeQuery(id+"F4.imprint","IMPRINT",FACE,{"disambiguationData":[TD([[makeQuery(id+"F4.imprint","IMPRINT",EDGE,{"disambiguationData":[TD([[subQ4,1.0]])],"derivedFrom":subQ3}),-1.0]])]});}
            var Q48;
            {var subQ3=sQuery(id+"F4.wireOp",EDGE,"E49");var subQ6=makeQuery(id+"F4.imprint","INTERSECT",VERTEX,{"derivedFrom":[sQuery(id+"F4.wireOp",EDGE,"E17"),subQ3]});Q48=makeQuery(id+"F4.imprint","IMPRINT",FACE,{"disambiguationData":[TD([[makeQuery(id+"F4.imprint","IMPRINT",EDGE,{"disambiguationData":[TD([[subQ6,1.0]])],"derivedFrom":subQ3}),1.0]])]});}
            var Q49;
            {var subQ3=sQuery(id+"F4.wireOp",EDGE,"E48");var subQ5=makeQuery(id+"F4.imprint","INTERSECT",VERTEX,{"derivedFrom":[sQuery(id+"F4.wireOp",EDGE,"E17"),subQ3]});Q49=makeQuery(id+"F4.imprint","IMPRINT",FACE,{"disambiguationData":[TD([[makeQuery(id+"F4.imprint","IMPRINT",EDGE,{"disambiguationData":[TD([[subQ5,-1.0]])],"derivedFrom":subQ3}),1.0]])]});}
            var Q50;
            {var subQ3=sQuery(id+"F4.wireOp",EDGE,"E47");var subQ6=makeQuery(id+"F4.imprint","INTERSECT",VERTEX,{"derivedFrom":[sQuery(id+"F4.wireOp",EDGE,"E17"),subQ3]});Q50=makeQuery(id+"F4.imprint","IMPRINT",FACE,{"disambiguationData":[TD([[makeQuery(id+"F4.imprint","IMPRINT",EDGE,{"disambiguationData":[TD([[subQ6,1.0]])],"derivedFrom":subQ3}),1.0]])]});}
            var Q51;
            {var subQ3=sQuery(id+"F4.wireOp",EDGE,"E46");var subQ6=makeQuery(id+"F4.imprint","INTERSECT",VERTEX,{"derivedFrom":[sQuery(id+"F4.wireOp",EDGE,"E17"),subQ3]});Q51=makeQuery(id+"F4.imprint","IMPRINT",FACE,{"disambiguationData":[TD([[makeQuery(id+"F4.imprint","IMPRINT",EDGE,{"disambiguationData":[TD([[subQ6,1.0]])],"derivedFrom":subQ3}),1.0]])]});}
            var Q52;
            {var subQ1=sQuery(id+"F4.wireOp",EDGE,"E23");var subQ3=sQuery(id+"F4.wireOp",EDGE,"E46");var subQ4=makeQuery(id+"F4.imprint","INTERSECT",VERTEX,{"disambiguationData":[OD(0.0)],"derivedFrom":[subQ1,subQ3]});Q52=makeQuery(id+"F4.imprint","IMPRINT",FACE,{"disambiguationData":[TD([[makeQuery(id+"F4.imprint","IMPRINT",EDGE,{"disambiguationData":[TD([[subQ4,-1.0]])],"derivedFrom":subQ3}),-1.0]])]});}
            var Q53;
            {var subQ1=sQuery(id+"F4.wireOp",EDGE,"E22");var subQ3=sQuery(id+"F4.wireOp",EDGE,"E49");var subQ4=makeQuery(id+"F4.imprint","INTERSECT",VERTEX,{"disambiguationData":[OD(1.0)],"derivedFrom":[subQ1,subQ3]});Q53=makeQuery(id+"F4.imprint","IMPRINT",FACE,{"disambiguationData":[TD([[makeQuery(id+"F4.imprint","IMPRINT",EDGE,{"disambiguationData":[TD([[subQ4,1.0]])],"derivedFrom":subQ3}),-1.0]])]});}
            var Q54;
            {var subQ1=sQuery(id+"F4.wireOp",EDGE,"E22");var subQ3=sQuery(id+"F4.wireOp",EDGE,"E49");var subQ4=makeQuery(id+"F4.imprint","INTERSECT",VERTEX,{"disambiguationData":[OD(0.0)],"derivedFrom":[subQ1,subQ3]});Q54=makeQuery(id+"F4.imprint","IMPRINT",FACE,{"disambiguationData":[TD([[makeQuery(id+"F4.imprint","IMPRINT",EDGE,{"disambiguationData":[TD([[subQ4,-1.0]])],"derivedFrom":subQ3}),-1.0]])]});}
            var Q55;
            {var subQ1=sQuery(id+"F4.wireOp",EDGE,"E25");var subQ3=sQuery(id+"F4.wireOp",EDGE,"E48");var subQ4=makeQuery(id+"F4.imprint","INTERSECT",VERTEX,{"disambiguationData":[OD(1.0)],"derivedFrom":[subQ1,subQ3]});Q55=makeQuery(id+"F4.imprint","IMPRINT",FACE,{"disambiguationData":[TD([[makeQuery(id+"F4.imprint","IMPRINT",EDGE,{"disambiguationData":[TD([[subQ4,1.0]])],"derivedFrom":subQ3}),-1.0]])]});}
            var Q56;
            {var subQ1=sQuery(id+"F4.wireOp",EDGE,"E25");var subQ3=sQuery(id+"F4.wireOp",EDGE,"E48");var subQ4=makeQuery(id+"F4.imprint","INTERSECT",VERTEX,{"disambiguationData":[OD(0.0)],"derivedFrom":[subQ1,subQ3]});Q56=makeQuery(id+"F4.imprint","IMPRINT",FACE,{"disambiguationData":[TD([[makeQuery(id+"F4.imprint","IMPRINT",EDGE,{"disambiguationData":[TD([[subQ4,-1.0]])],"derivedFrom":subQ3}),-1.0]])]});}
            var Q57;
            {var subQ1=sQuery(id+"F4.wireOp",EDGE,"E24");var subQ3=sQuery(id+"F4.wireOp",EDGE,"E47");var subQ4=makeQuery(id+"F4.imprint","INTERSECT",VERTEX,{"disambiguationData":[OD(1.0)],"derivedFrom":[subQ1,subQ3]});Q57=makeQuery(id+"F4.imprint","IMPRINT",FACE,{"disambiguationData":[TD([[makeQuery(id+"F4.imprint","IMPRINT",EDGE,{"disambiguationData":[TD([[subQ4,1.0]])],"derivedFrom":subQ3}),-1.0]])]});}
            var Q58;
            {var subQ1=sQuery(id+"F4.wireOp",EDGE,"E24");var subQ3=sQuery(id+"F4.wireOp",EDGE,"E47");var subQ4=makeQuery(id+"F4.imprint","INTERSECT",VERTEX,{"disambiguationData":[OD(0.0)],"derivedFrom":[subQ1,subQ3]});Q58=makeQuery(id+"F4.imprint","IMPRINT",FACE,{"disambiguationData":[TD([[makeQuery(id+"F4.imprint","IMPRINT",EDGE,{"disambiguationData":[TD([[subQ4,-1.0]])],"derivedFrom":subQ3}),-1.0]])]});}
            var Q59;
            {var subQ1=sQuery(id+"F4.wireOp",EDGE,"E23");var subQ3=sQuery(id+"F4.wireOp",EDGE,"E46");var subQ4=makeQuery(id+"F4.imprint","INTERSECT",VERTEX,{"disambiguationData":[OD(1.0)],"derivedFrom":[subQ1,subQ3]});Q59=makeQuery(id+"F4.imprint","IMPRINT",FACE,{"disambiguationData":[TD([[makeQuery(id+"F4.imprint","IMPRINT",EDGE,{"disambiguationData":[TD([[subQ4,1.0]])],"derivedFrom":subQ3}),-1.0]])]});}
            var Q60;
            {var subQ5=sQuery(id+"F4.wireOp",EDGE,"E40");var subQ6=sQuery(id+"F4.wireOp",EDGE,"E33");var subQ7=makeQuery(id+"F4.imprint","INTERSECT",VERTEX,{"derivedFrom":[subQ6,subQ5]});Q60=makeQuery(id+"F4.imprint","IMPRINT",FACE,{"disambiguationData":[TD([[makeQuery(id+"F4.imprint","IMPRINT",EDGE,{"disambiguationData":[TD([[subQ7,-1.0]])],"derivedFrom":subQ6}),-1.0]])]});}
            var Q61;
            {var subQ3=sQuery(id+"F4.wireOp",EDGE,"E55");var subQ7=sQuery(id+"F4.wireOp",EDGE,"E31");var subQ9=makeQuery(id+"F4.imprint","INTERSECT",VERTEX,{"disambiguationData":[OD(1.0)],"derivedFrom":[subQ7,subQ3]});Q61=makeQuery(id+"F4.imprint","IMPRINT",FACE,{"disambiguationData":[TD([[makeQuery(id+"F4.imprint","IMPRINT",EDGE,{"disambiguationData":[TD([[subQ9,-1.0]])],"derivedFrom":subQ7}),-1.0]])]});}
            var Q62;
            {var subQ3=sQuery(id+"F4.wireOp",EDGE,"E30");var subQ7=sQuery(id+"F4.wireOp",EDGE,"E55");var subQ9=makeQuery(id+"F4.imprint","INTERSECT",VERTEX,{"disambiguationData":[OD(0.0)],"derivedFrom":[subQ3,subQ7]});Q62=makeQuery(id+"F4.imprint","IMPRINT",FACE,{"disambiguationData":[TD([[makeQuery(id+"F4.imprint","IMPRINT",EDGE,{"disambiguationData":[TD([[subQ9,1.0]])],"derivedFrom":subQ3}),-1.0]])]});}
            var Q63;
            {var subQ3=sQuery(id+"F4.wireOp",EDGE,"E52");var subQ5=sQuery(id+"F4.wireOp",EDGE,"E32");var subQ6=makeQuery(id+"F4.imprint","INTERSECT",VERTEX,{"disambiguationData":[OD(1.0)],"derivedFrom":[subQ5,subQ3]});Q63=makeQuery(id+"F4.imprint","IMPRINT",FACE,{"disambiguationData":[TD([[makeQuery(id+"F4.imprint","IMPRINT",EDGE,{"disambiguationData":[TD([[subQ6,-1.0]])],"derivedFrom":subQ5}),-1.0]])]});}
            var Q64;
            {var subQ0=sQuery(id+"F4.wireOp",EDGE,"E38");var subQ3=sQuery(id+"F4.wireOp",EDGE,"E31");var subQ4=makeQuery(id+"F4.imprint","INTERSECT",VERTEX,{"derivedFrom":[subQ3,subQ0]});Q64=makeQuery(id+"F4.imprint","IMPRINT",FACE,{"disambiguationData":[TD([[makeQuery(id+"F4.imprint","IMPRINT",EDGE,{"disambiguationData":[TD([[subQ4,-1.0]])],"derivedFrom":subQ3}),-1.0]])]});}
            var Q65;
            {var subQ5=sQuery(id+"F4.wireOp",EDGE,"E39");var subQ7=sQuery(id+"F4.wireOp",EDGE,"E33");var subQ8=makeQuery(id+"F4.imprint","INTERSECT",VERTEX,{"derivedFrom":[subQ7,subQ5]});Q65=makeQuery(id+"F4.imprint","IMPRINT",FACE,{"disambiguationData":[TD([[makeQuery(id+"F4.imprint","IMPRINT",EDGE,{"disambiguationData":[TD([[subQ8,1.0]])],"derivedFrom":subQ7}),-1.0]])]});}
            var Q66;
            {var subQ5=sQuery(id+"F4.wireOp",EDGE,"E39");var subQ7=sQuery(id+"F4.wireOp",EDGE,"E32");var subQ8=makeQuery(id+"F4.imprint","INTERSECT",VERTEX,{"derivedFrom":[subQ7,subQ5]});Q66=makeQuery(id+"F4.imprint","IMPRINT",FACE,{"disambiguationData":[TD([[makeQuery(id+"F4.imprint","IMPRINT",EDGE,{"disambiguationData":[TD([[subQ8,-1.0]])],"derivedFrom":subQ7}),-1.0]])]});}
            var Q67;
            {var subQ3=sQuery(id+"F4.wireOp",EDGE,"E54");var subQ7=sQuery(id+"F4.wireOp",EDGE,"E30");var subQ9=makeQuery(id+"F4.imprint","INTERSECT",VERTEX,{"disambiguationData":[OD(1.0)],"derivedFrom":[subQ7,subQ3]});Q67=makeQuery(id+"F4.imprint","IMPRINT",FACE,{"disambiguationData":[TD([[makeQuery(id+"F4.imprint","IMPRINT",EDGE,{"disambiguationData":[TD([[subQ9,-1.0]])],"derivedFrom":subQ7}),-1.0]])]});}
            var Q68;
            {var subQ0=sQuery(id+"F4.wireOp",EDGE,"E33");var subQ3=sQuery(id+"F4.wireOp",EDGE,"E40");var subQ5=makeQuery(id+"F4.imprint","INTERSECT",VERTEX,{"derivedFrom":[subQ0,subQ3]});Q68=makeQuery(id+"F4.imprint","IMPRINT",FACE,{"disambiguationData":[TD([[makeQuery(id+"F4.imprint","IMPRINT",EDGE,{"disambiguationData":[TD([[subQ5,-1.0]])],"derivedFrom":subQ3}),-1.0]])]});}
            var Q69;
            {var subQ0=sQuery(id+"F4.wireOp",EDGE,"E31");var subQ3=sQuery(id+"F4.wireOp",EDGE,"E41");var subQ5=makeQuery(id+"F4.imprint","INTERSECT",VERTEX,{"derivedFrom":[subQ0,subQ3]});Q69=makeQuery(id+"F4.imprint","IMPRINT",FACE,{"disambiguationData":[TD([[makeQuery(id+"F4.imprint","IMPRINT",EDGE,{"disambiguationData":[TD([[subQ5,1.0]])],"derivedFrom":subQ3}),-1.0]])]});}
            var Q70;
            {var subQ0=sQuery(id+"F4.wireOp",EDGE,"E30");var subQ3=sQuery(id+"F4.wireOp",EDGE,"E41");var subQ5=makeQuery(id+"F4.imprint","INTERSECT",VERTEX,{"derivedFrom":[subQ0,subQ3]});Q70=makeQuery(id+"F4.imprint","IMPRINT",FACE,{"disambiguationData":[TD([[makeQuery(id+"F4.imprint","IMPRINT",EDGE,{"disambiguationData":[TD([[subQ5,-1.0]])],"derivedFrom":subQ3}),-1.0]])]});}
            var Q71;
            {var subQ0=sQuery(id+"F4.wireOp",EDGE,"E32");var subQ3=sQuery(id+"F4.wireOp",EDGE,"E38");var subQ5=makeQuery(id+"F4.imprint","INTERSECT",VERTEX,{"derivedFrom":[subQ0,subQ3]});Q71=makeQuery(id+"F4.imprint","IMPRINT",FACE,{"disambiguationData":[TD([[makeQuery(id+"F4.imprint","IMPRINT",EDGE,{"disambiguationData":[TD([[subQ5,1.0]])],"derivedFrom":subQ3}),-1.0]])]});}
            var Q72;
            {var subQ0=sQuery(id+"F4.wireOp",EDGE,"E33");var subQ3=sQuery(id+"F4.wireOp",EDGE,"E39");var subQ5=makeQuery(id+"F4.imprint","INTERSECT",VERTEX,{"derivedFrom":[subQ0,subQ3]});Q72=makeQuery(id+"F4.imprint","IMPRINT",FACE,{"disambiguationData":[TD([[makeQuery(id+"F4.imprint","IMPRINT",EDGE,{"disambiguationData":[TD([[subQ5,-1.0]])],"derivedFrom":subQ3}),1.0]])]});}
            var Q73;
            {var subQ0=sQuery(id+"F4.wireOp",EDGE,"E31");var subQ3=sQuery(id+"F4.wireOp",EDGE,"E38");var subQ5=makeQuery(id+"F4.imprint","INTERSECT",VERTEX,{"derivedFrom":[subQ0,subQ3]});Q73=makeQuery(id+"F4.imprint","IMPRINT",FACE,{"disambiguationData":[TD([[makeQuery(id+"F4.imprint","IMPRINT",EDGE,{"disambiguationData":[TD([[subQ5,-1.0]])],"derivedFrom":subQ3}),-1.0]])]});}
            var Q74;
            {var subQ0=sQuery(id+"F4.wireOp",EDGE,"E30");var subQ3=sQuery(id+"F4.wireOp",EDGE,"E40");var subQ5=makeQuery(id+"F4.imprint","INTERSECT",VERTEX,{"derivedFrom":[subQ0,subQ3]});Q74=makeQuery(id+"F4.imprint","IMPRINT",FACE,{"disambiguationData":[TD([[makeQuery(id+"F4.imprint","IMPRINT",EDGE,{"disambiguationData":[TD([[subQ5,1.0]])],"derivedFrom":subQ3}),-1.0]])]});}
            var Q75;
            {var subQ0=sQuery(id+"F4.wireOp",EDGE,"E32");var subQ3=sQuery(id+"F4.wireOp",EDGE,"E39");var subQ5=makeQuery(id+"F4.imprint","INTERSECT",VERTEX,{"derivedFrom":[subQ0,subQ3]});Q75=makeQuery(id+"F4.imprint","IMPRINT",FACE,{"disambiguationData":[TD([[makeQuery(id+"F4.imprint","IMPRINT",EDGE,{"disambiguationData":[TD([[subQ5,1.0]])],"derivedFrom":subQ3}),1.0]])]});}
            extrude(context, id + "F5", {"entities" : qUnion([Q0, Q1, Q2, Q3, Q4, Q5, Q6, Q7, Q8, Q9, Q10, Q11, Q12, Q13, Q14, Q15, Q16, Q17, Q18, Q19, Q20, Q21, Q22, Q23, Q24, Q25, Q26, Q27, Q28, Q29, Q30, Q31, Q32, Q33, Q34, Q35, Q36, Q37, Q38, Q39, Q40, Q41, Q42, Q43, Q44, Q45, Q46, Q47, Q48, Q49, Q50, Q51, Q52, Q53, Q54, Q55, Q56, Q57, Q58, Q59, Q60, Q61, Q62, Q63, Q64, Q65, Q66, Q67, Q68, Q69, Q70, Q71, Q72, Q73, Q74, Q75]), "endBound" : BoundingType.SYMMETRIC, "depth" : 25 * mm, "offsetDistance" : 25 * mm});
        }
        {
            var Q0;
            Q0=makeQuery(id+"F1.opExtrude","CAP_FACE",FACE,{"disambiguationData":[OSD([sQuery(id+"F0.wireOp",EDGE,"E0.left"),sQuery(id+"F0.wireOp",EDGE,"E0.right"),sQuery(id+"F0.wireOp",EDGE,"E1"),sQuery(id+"F0.wireOp",EDGE,"E3"),sQuery(id+"F0.wireOp",EDGE,"E4")])],"isStart":false});
            var sketch = newSketch(context, id + "F6", { "sketchPlane" : qUnion([Q0])});
            skLineSegment(sketch, "E56", {"start": v(0, 31.87) * mm, "end": v(0, 22.5) * mm});
            skLineSegment(sketch, "E57", {"start": v(0, 22.5) * mm, "end": v(-17.5, 14.14) * mm});
            skLineSegment(sketch, "E58", {"start": v(0, 22.5) * mm, "end": v(17.5, 14.14) * mm});
            skLineSegment(sketch, "E59", {"start": v(17.5, 14.14) * mm, "end": v(0, 31.87) * mm});
            skLineSegment(sketch, "E60", {"start": v(0, 31.87) * mm, "end": v(-17.5, 14.14) * mm});
            skLineSegment(sketch, "E61", {"start": v(-7.25, 26.44) * mm, "end": v(0, 22.5) * mm});
            skLineSegment(sketch, "E62", {"start": v(0, 22.5) * mm, "end": v(7.25, 26.44) * mm});
            skLineSegment(sketch, "E63", {"start": v(-16.7, 18.35) * mm, "end": v(0, 27.19) * mm});
            skLineSegment(sketch, "E64", {"start": v(16.7, 18.35) * mm, "end": v(0, 27.19) * mm});
            skArc(sketch, "E65", {"start": v(0, 22.5) * mm, "mid": v(3.75, 24.38) * mm, "end": v(4.5, 28.5) * mm});
            skArc(sketch, "E66", {"start": v(0, 22.5) * mm, "mid": v(-3.75, 24.38) * mm, "end": v(-4.5, 28.5) * mm});
            skLineSegment(sketch, "E67", {"start": v(-4.5, 28.5) * mm, "end": v(4.5, 28.5) * mm});
            skFitSpline(sketch, "E68", {"points": [v(-4.14, 25) * mm, v(0, 28.5) * mm, v(4.14, 25) * mm], "startDerivative": vector(8.29, 10.51) * mm, "endDerivative": vector(8.29, -10.51) * mm});
            skSolve(sketch);
        }
        {
            var Q0;
            {var subQ0=sQuery(id+"F6.wireOp",EDGE,"E66");var subQ1=sQuery(id+"F6.wireOp",EDGE,"E61");var subQ5=makeQuery(id+"F6.imprint","INTERSECT",VERTEX,{"derivedFrom":[subQ1,subQ0]});Q0=makeQuery(id+"F6.imprint","IMPRINT",FACE,{"disambiguationData":[TD([[makeQuery(id+"F6.imprint","IMPRINT",EDGE,{"disambiguationData":[TD([[subQ5,-1.0]])],"derivedFrom":subQ1}),-1.0]])]});}
            var Q1;
            {var subQ0=sQuery(id+"F6.wireOp",EDGE,"E65");var subQ1=sQuery(id+"F6.wireOp",EDGE,"E62");var subQ5=makeQuery(id+"F6.imprint","INTERSECT",VERTEX,{"derivedFrom":[subQ1,subQ0]});Q1=makeQuery(id+"F6.imprint","IMPRINT",FACE,{"disambiguationData":[TD([[makeQuery(id+"F6.imprint","IMPRINT",EDGE,{"disambiguationData":[TD([[subQ5,1.0]])],"derivedFrom":subQ1}),-1.0]])]});}
            var Q2;
            {var subQ0=sQuery(id+"F6.wireOp",EDGE,"E64");var subQ1=sQuery(id+"F6.wireOp",EDGE,"E59");var subQ2=makeQuery(id+"F6.imprint","INTERSECT",VERTEX,{"derivedFrom":[subQ1,subQ0]});Q2=makeQuery(id+"F6.imprint","IMPRINT",FACE,{"disambiguationData":[TD([[makeQuery(id+"F6.imprint","IMPRINT",EDGE,{"disambiguationData":[TD([[subQ2,-1.0]])],"derivedFrom":subQ1}),1.0]])]});}
            var Q3;
            {var subQ0=sQuery(id+"F6.wireOp",EDGE,"E62");var subQ1=sQuery(id+"F6.wireOp",EDGE,"E59");var subQ2=makeQuery(id+"F6.imprint","INTERSECT",VERTEX,{"derivedFrom":[subQ1,subQ0]});Q3=makeQuery(id+"F6.imprint","IMPRINT",FACE,{"disambiguationData":[TD([[makeQuery(id+"F6.imprint","IMPRINT",EDGE,{"disambiguationData":[TD([[subQ2,-1.0]])],"derivedFrom":subQ1}),1.0]])]});}
            var Q4;
            {var subQ0=sQuery(id+"F6.wireOp",EDGE,"E61");var subQ1=sQuery(id+"F6.wireOp",EDGE,"E60");var subQ2=makeQuery(id+"F6.imprint","INTERSECT",VERTEX,{"derivedFrom":[subQ1,subQ0]});Q4=makeQuery(id+"F6.imprint","IMPRINT",FACE,{"disambiguationData":[TD([[makeQuery(id+"F6.imprint","IMPRINT",EDGE,{"disambiguationData":[TD([[subQ2,-1.0]])],"derivedFrom":subQ1}),1.0]])]});}
            var Q5;
            {var subQ0=sQuery(id+"F6.wireOp",EDGE,"E66");var subQ1=sQuery(id+"F6.wireOp",EDGE,"E60");var subQ2=makeQuery(id+"F6.imprint","INTERSECT",VERTEX,{"derivedFrom":[subQ1,subQ0]});Q5=makeQuery(id+"F6.imprint","IMPRINT",FACE,{"disambiguationData":[TD([[makeQuery(id+"F6.imprint","IMPRINT",EDGE,{"disambiguationData":[TD([[subQ2,-1.0]])],"derivedFrom":subQ1}),1.0]])]});}
            var Q6;
            {var subQ1=sQuery(id+"F6.wireOp",EDGE,"E56");var subQ5=sQuery(id+"F6.wireOp",EDGE,"E67");var subQ6=makeQuery(id+"F6.imprint","INTERSECT",VERTEX,{"derivedFrom":[subQ1,subQ5]});Q6=makeQuery(id+"F6.imprint","IMPRINT",FACE,{"disambiguationData":[TD([[makeQuery(id+"F6.imprint","IMPRINT",EDGE,{"disambiguationData":[TD([[subQ6,1.0]])],"derivedFrom":subQ5}),1.0]])]});}
            var Q7;
            {var subQ1=sQuery(id+"F6.wireOp",EDGE,"E56");var subQ5=sQuery(id+"F6.wireOp",EDGE,"E67");var subQ6=makeQuery(id+"F6.imprint","INTERSECT",VERTEX,{"derivedFrom":[subQ1,subQ5]});Q7=makeQuery(id+"F6.imprint","IMPRINT",FACE,{"disambiguationData":[TD([[makeQuery(id+"F6.imprint","IMPRINT",EDGE,{"disambiguationData":[TD([[subQ6,-1.0]])],"derivedFrom":subQ5}),1.0]])]});}
            var Q8;
            {var subQ2=sQuery(id+"F0.wireOp",EDGE,"E0.right");var subQ4=makeQuery(id+"F0.imprint","INTERSECT",VERTEX,{"derivedFrom":[subQ2,sQuery(id+"F0.wireOp",EDGE,"E10")]});var subQ5=sQuery(id+"F0.wireOp",EDGE,"E1");var subQ6=makeQuery(id+"F0.imprint","INTERSECT",VERTEX,{"derivedFrom":[subQ2,subQ5]});var subQ7=makeQuery(id+"F3.opShell","OFFSET_EDGE",EDGE,{"disambiguationData":[OSD([subQ2]),TDD([makeQuery(id+"F1.opExtrude","CAP_EDGE",EDGE,{"disambiguationData":[OSD([subQ2]),TDD([makeQuery(id+"F0.imprint","IMPRINT",EDGE,{"disambiguationData":[TD([[subQ6,1.0]])],"derivedFrom":subQ2}),makeQuery(id+"F0.imprint","IMPRINT",EDGE,{"disambiguationData":[TD([[subQ4,1.0]])],"derivedFrom":subQ2})])],"isStart":false})])]});Q8=makeQuery(id+"F6.imprint","IMPRINT",FACE,{"disambiguationData":[TD([[makeQuery(id+"F6.imprint","IMPRINT",EDGE,{"derivedFrom":subQ7}),-1.0]])]});}
            var Q9;
            {var subQ2=sQuery(id+"F0.wireOp",EDGE,"E0.left");var subQ4=makeQuery(id+"F0.imprint","INTERSECT",VERTEX,{"derivedFrom":[subQ2,sQuery(id+"F0.wireOp",EDGE,"E14")]});var subQ5=sQuery(id+"F0.wireOp",EDGE,"E1");var subQ6=makeQuery(id+"F0.imprint","INTERSECT",VERTEX,{"derivedFrom":[subQ2,subQ5]});var subQ7=makeQuery(id+"F3.opShell","OFFSET_EDGE",EDGE,{"disambiguationData":[OSD([subQ2]),TDD([makeQuery(id+"F1.opExtrude","CAP_EDGE",EDGE,{"disambiguationData":[OSD([subQ2]),TDD([makeQuery(id+"F0.imprint","IMPRINT",EDGE,{"disambiguationData":[TD([[subQ6,1.0]])],"derivedFrom":subQ2}),makeQuery(id+"F0.imprint","IMPRINT",EDGE,{"disambiguationData":[TD([[subQ4,1.0]])],"derivedFrom":subQ2})])],"isStart":false})])]});Q9=makeQuery(id+"F6.imprint","IMPRINT",FACE,{"disambiguationData":[TD([[makeQuery(id+"F6.imprint","IMPRINT",EDGE,{"derivedFrom":subQ7}),1.0]])]});}
            var Q10;
            {var subQ0=sQuery(id+"F6.wireOp",EDGE,"E63");var subQ1=sQuery(id+"F6.wireOp",EDGE,"E56");var subQ2=makeQuery(id+"F6.imprint","INTERSECT",VERTEX,{"derivedFrom":[subQ1,subQ0,sQuery(id+"F6.wireOp",EDGE,"E64")]});Q10=makeQuery(id+"F6.imprint","IMPRINT",FACE,{"disambiguationData":[TD([[makeQuery(id+"F6.imprint","IMPRINT",EDGE,{"disambiguationData":[TD([[subQ2,1.0]])],"derivedFrom":subQ1}),-1.0]])]});}
            var Q11;
            {var subQ0=sQuery(id+"F6.wireOp",EDGE,"E64");var subQ1=sQuery(id+"F6.wireOp",EDGE,"E56");var subQ2=makeQuery(id+"F6.imprint","INTERSECT",VERTEX,{"derivedFrom":[subQ1,sQuery(id+"F6.wireOp",EDGE,"E63"),subQ0]});Q11=makeQuery(id+"F6.imprint","IMPRINT",FACE,{"disambiguationData":[TD([[makeQuery(id+"F6.imprint","IMPRINT",EDGE,{"disambiguationData":[TD([[subQ2,1.0]])],"derivedFrom":subQ1}),1.0]])]});}
            extrude(context, id + "F7", {"entities" : qUnion([Q0, Q1, Q2, Q3, Q4, Q5, Q6, Q7, Q8, Q9, Q10, Q11]), "oppositeDirection" : true, "depth" : 25 * mm, "offsetDistance" : 25 * mm});
        }
        {
            var Q0;
            {var subQ3=sQuery(id+"F0.wireOp",EDGE,"E14");Q0=makeQuery(id+"F0.imprint","IMPRINT",FACE,{"disambiguationData":[TD([[makeQuery(id+"F0.imprint","IMPRINT",EDGE,{"derivedFrom":subQ3}),1.0]])]});}
            var Q1;
            {var subQ3=sQuery(id+"F0.wireOp",EDGE,"E10");Q1=makeQuery(id+"F0.imprint","IMPRINT",FACE,{"disambiguationData":[TD([[makeQuery(id+"F0.imprint","IMPRINT",EDGE,{"derivedFrom":subQ3}),-1.0]])]});}
            extrude(context, id + "F8", {"entities" : qUnion([Q0, Q1]), "endBound" : BoundingType.SYMMETRIC, "depth" : 25 * mm, "offsetDistance" : 25 * mm});
        }
        {
            var Q0;
            Q0=makeQuery(id+"F1.opExtrude","SWEPT_EDGE",EDGE,{"disambiguationData":[OSD([sQuery(id+"F0.wireOp",EDGE,"E0.top"),sQuery(id+"F0.wireOp",EDGE,"E0.left")])]});
            var Q1;
            Q1=makeQuery(id+"F1.opExtrude","SWEPT_EDGE",EDGE,{"disambiguationData":[OSD([sQuery(id+"F0.wireOp",EDGE,"E0.top"),sQuery(id+"F0.wireOp",EDGE,"E0.right")])]});
            fillet(context, id + "F9", {"entities" : qUnion([Q0, Q1]), "radius" : 5 * mm, "tangentPropagation" : true, "allowEdgeOverflow" : false});
        }
        {
            var Q0;
            Q0=makeQuery(id+"F8.opExtrude","CAP_FACE",FACE,{"disambiguationData":[OSD([sQuery(id+"F0.wireOp",EDGE,"E0.left"),sQuery(id+"F0.wireOp",EDGE,"E14"),sQuery(id+"F0.wireOp",EDGE,"E15")])],"isStart":false});
            var Q1;
            Q1=makeQuery(id+"F8.opExtrude","CAP_FACE",FACE,{"disambiguationData":[OSD([sQuery(id+"F0.wireOp",EDGE,"E0.right"),sQuery(id+"F0.wireOp",EDGE,"E10"),sQuery(id+"F0.wireOp",EDGE,"E11")])],"isStart":false});
            var Q2;
            Q2=makeQuery(id+"F8.opExtrude","CAP_FACE",FACE,{"disambiguationData":[OSD([sQuery(id+"F0.wireOp",EDGE,"E0.left"),sQuery(id+"F0.wireOp",EDGE,"E14"),sQuery(id+"F0.wireOp",EDGE,"E15")])],"isStart":true});
            var Q3;
            Q3=makeQuery(id+"F8.opExtrude","CAP_FACE",FACE,{"disambiguationData":[OSD([sQuery(id+"F0.wireOp",EDGE,"E0.right"),sQuery(id+"F0.wireOp",EDGE,"E10"),sQuery(id+"F0.wireOp",EDGE,"E11")])],"isStart":true});
            shell(context, id + "F10", {"entities" : qUnion([Q0, Q1, Q2, Q3]), "thickness" : 1 * mm});
        }
        {
            var Q0;
            Q0=makeQuery(id+"F8.opExtrude","CAP_FACE",FACE,{"disambiguationData":[OSD([sQuery(id+"F0.wireOp",EDGE,"E0.left"),sQuery(id+"F0.wireOp",EDGE,"E14"),sQuery(id+"F0.wireOp",EDGE,"E15")])],"isStart":false});
            var sketch = newSketch(context, id + "F11", { "sketchPlane" : qUnion([Q0])});
            skLineSegment(sketch, "E69", {"start": v(-21, -14.43) * mm, "end": v(-25.97, -6.78) * mm});
            skLineSegment(sketch, "E70", {"start": v(-25.97, -6.78) * mm, "end": v(-21, -3.8) * mm});
            skLineSegment(sketch, "E71", {"start": v(-21, -3.8) * mm, "end": v(-30.95, -20.41) * mm});
            skLineSegment(sketch, "E72", {"start": v(-21, 6.84) * mm, "end": v(-25.97, -17.42) * mm});
            skLineSegment(sketch, "E73", {"start": v(-25.97, -17.42) * mm, "end": v(-21, 0) * mm});
            skLineSegment(sketch, "E74", {"start": v(-21, 0) * mm, "end": v(-25.97, -6.78) * mm});
            skLineSegment(sketch, "E75", {"start": v(-21, 0) * mm, "end": v(-30.95, -20.41) * mm});
            skLineSegment(sketch, "E76", {"start": v(-21, -14.43) * mm, "end": v(-23.49, -5.3) * mm});
            skSolve(sketch);
        }
        {
            var Q0;
            Q0=makeQuery(id+"F8.opExtrude","CAP_FACE",FACE,{"disambiguationData":[OSD([sQuery(id+"F0.wireOp",EDGE,"E0.right"),sQuery(id+"F0.wireOp",EDGE,"E10"),sQuery(id+"F0.wireOp",EDGE,"E11")])],"isStart":false});
            var sketch = newSketch(context, id + "F12", { "sketchPlane" : qUnion([Q0])});
            skLineSegment(sketch, "E77", {"start": v(21, -14.43) * mm, "end": v(25.97, -6.78) * mm});
            skLineSegment(sketch, "E78", {"start": v(25.97, -6.78) * mm, "end": v(21, -3.55) * mm});
            skLineSegment(sketch, "E79", {"start": v(21, -3.55) * mm, "end": v(30.95, -20.41) * mm});
            skLineSegment(sketch, "E80", {"start": v(30.95, -20.41) * mm, "end": v(21, 0) * mm});
            skLineSegment(sketch, "E81", {"start": v(21, 0) * mm, "end": v(25.97, -17.42) * mm});
            skLineSegment(sketch, "E82", {"start": v(25.97, -17.42) * mm, "end": v(21, 6.84) * mm});
            skLineSegment(sketch, "E83", {"start": v(21, 0) * mm, "end": v(25.97, -6.78) * mm});
            skLineSegment(sketch, "E84", {"start": v(21, -14.43) * mm, "end": v(23.46, -5.15) * mm});
            skSolve(sketch);
        }
        {
            var Q0;
            {var subQ0=sQuery(id+"F11.wireOp",EDGE,"E73");var subQ1=sQuery(id+"F11.wireOp",EDGE,"E69");var subQ2=makeQuery(id+"F11.imprint","INTERSECT",VERTEX,{"derivedFrom":[subQ1,subQ0]});Q0=makeQuery(id+"F11.imprint","IMPRINT",FACE,{"disambiguationData":[TD([[makeQuery(id+"F11.imprint","IMPRINT",EDGE,{"disambiguationData":[TD([[subQ2,-1.0]])],"derivedFrom":subQ1}),1.0]])]});}
            var Q1;
            {var subQ0=sQuery(id+"F11.wireOp",EDGE,"E75");var subQ1=sQuery(id+"F11.wireOp",EDGE,"E69");var subQ2=makeQuery(id+"F11.imprint","INTERSECT",VERTEX,{"derivedFrom":[subQ1,subQ0]});Q1=makeQuery(id+"F11.imprint","IMPRINT",FACE,{"disambiguationData":[TD([[makeQuery(id+"F11.imprint","IMPRINT",EDGE,{"disambiguationData":[TD([[subQ2,1.0]])],"derivedFrom":subQ1}),1.0]])]});}
            var Q2;
            {var subQ0=sQuery(id+"F11.wireOp",EDGE,"E76");var subQ7=sQuery(id+"F11.wireOp",EDGE,"E71");var subQ8=makeQuery(id+"F11.imprint","INTERSECT",VERTEX,{"derivedFrom":[subQ7,subQ0]});Q2=makeQuery(id+"F11.imprint","IMPRINT",FACE,{"disambiguationData":[TD([[makeQuery(id+"F11.imprint","IMPRINT",EDGE,{"disambiguationData":[TD([[subQ8,-1.0]])],"derivedFrom":subQ7}),1.0]])]});}
            var Q3;
            {var subQ1=sQuery(id+"F11.wireOp",EDGE,"E69");var subQ4=sQuery(id+"F11.wireOp",EDGE,"E75");var subQ5=makeQuery(id+"F11.imprint","INTERSECT",VERTEX,{"derivedFrom":[subQ1,subQ4]});Q3=makeQuery(id+"F11.imprint","IMPRINT",FACE,{"disambiguationData":[TD([[makeQuery(id+"F11.imprint","IMPRINT",EDGE,{"disambiguationData":[TD([[subQ5,1.0]])],"derivedFrom":subQ4}),-1.0]])]});}
            var Q4;
            {var subQ0=sQuery(id+"F11.wireOp",EDGE,"E73");var subQ1=sQuery(id+"F11.wireOp",EDGE,"E71");var subQ2=makeQuery(id+"F11.imprint","INTERSECT",VERTEX,{"derivedFrom":[subQ1,subQ0]});Q4=makeQuery(id+"F11.imprint","IMPRINT",FACE,{"disambiguationData":[TD([[makeQuery(id+"F11.imprint","IMPRINT",EDGE,{"disambiguationData":[TD([[subQ2,-1.0]])],"derivedFrom":subQ0}),1.0]])]});}
            var Q5;
            {var subQ1=sQuery(id+"F11.wireOp",EDGE,"E70");var subQ4=sQuery(id+"F11.wireOp",EDGE,"E73");var subQ5=makeQuery(id+"F11.imprint","INTERSECT",VERTEX,{"derivedFrom":[subQ1,subQ4]});Q5=makeQuery(id+"F11.imprint","IMPRINT",FACE,{"disambiguationData":[TD([[makeQuery(id+"F11.imprint","IMPRINT",EDGE,{"disambiguationData":[TD([[subQ5,1.0]])],"derivedFrom":subQ4}),-1.0]])]});}
            var Q6;
            {var subQ1=sQuery(id+"F11.wireOp",EDGE,"E70");var subQ3=sQuery(id+"F11.wireOp",EDGE,"E73");var subQ4=makeQuery(id+"F11.imprint","INTERSECT",VERTEX,{"derivedFrom":[subQ1,subQ3]});Q6=makeQuery(id+"F11.imprint","IMPRINT",FACE,{"disambiguationData":[TD([[makeQuery(id+"F11.imprint","IMPRINT",EDGE,{"disambiguationData":[TD([[subQ4,1.0]])],"derivedFrom":subQ1}),1.0]])]});}
            var Q7;
            {var subQ0=sQuery(id+"F11.wireOp",EDGE,"E72");var subQ5=sQuery(id+"F11.wireOp",EDGE,"E74");var subQ6=makeQuery(id+"F11.imprint","INTERSECT",VERTEX,{"derivedFrom":[subQ0,subQ5]});Q7=makeQuery(id+"F11.imprint","IMPRINT",FACE,{"disambiguationData":[TD([[makeQuery(id+"F11.imprint","IMPRINT",EDGE,{"disambiguationData":[TD([[subQ6,1.0]])],"derivedFrom":subQ0}),-1.0]])]});}
            var Q8;
            {var subQ0=sQuery(id+"F12.wireOp",EDGE,"E82");var subQ5=sQuery(id+"F12.wireOp",EDGE,"E83");var subQ6=makeQuery(id+"F12.imprint","INTERSECT",VERTEX,{"derivedFrom":[subQ0,subQ5]});Q8=makeQuery(id+"F12.imprint","IMPRINT",FACE,{"disambiguationData":[TD([[makeQuery(id+"F12.imprint","IMPRINT",EDGE,{"disambiguationData":[TD([[subQ6,-1.0]])],"derivedFrom":subQ0}),-1.0]])]});}
            var Q9;
            {var subQ1=sQuery(id+"F12.wireOp",EDGE,"E77");var subQ5=sQuery(id+"F12.wireOp",EDGE,"E81");var subQ6=makeQuery(id+"F12.imprint","INTERSECT",VERTEX,{"derivedFrom":[subQ1,subQ5]});Q9=makeQuery(id+"F12.imprint","IMPRINT",FACE,{"disambiguationData":[TD([[makeQuery(id+"F12.imprint","IMPRINT",EDGE,{"disambiguationData":[TD([[subQ6,1.0]])],"derivedFrom":subQ5}),-1.0]])]});}
            var Q10;
            {var subQ0=sQuery(id+"F12.wireOp",EDGE,"E79");var subQ1=sQuery(id+"F12.wireOp",EDGE,"E77");var subQ2=makeQuery(id+"F12.imprint","INTERSECT",VERTEX,{"derivedFrom":[subQ1,subQ0]});Q10=makeQuery(id+"F12.imprint","IMPRINT",FACE,{"disambiguationData":[TD([[makeQuery(id+"F12.imprint","IMPRINT",EDGE,{"disambiguationData":[TD([[subQ2,-1.0]])],"derivedFrom":subQ1}),-1.0]])]});}
            var Q11;
            {var subQ0=sQuery(id+"F12.wireOp",EDGE,"E81");var subQ1=sQuery(id+"F12.wireOp",EDGE,"E77");var subQ2=makeQuery(id+"F12.imprint","INTERSECT",VERTEX,{"derivedFrom":[subQ1,subQ0]});Q11=makeQuery(id+"F12.imprint","IMPRINT",FACE,{"disambiguationData":[TD([[makeQuery(id+"F12.imprint","IMPRINT",EDGE,{"disambiguationData":[TD([[subQ2,-1.0]])],"derivedFrom":subQ1}),-1.0]])]});}
            var Q12;
            {var subQ0=sQuery(id+"F12.wireOp",EDGE,"E84");var subQ1=sQuery(id+"F12.wireOp",EDGE,"E79");var subQ2=makeQuery(id+"F12.imprint","INTERSECT",VERTEX,{"derivedFrom":[subQ1,subQ0]});Q12=makeQuery(id+"F12.imprint","IMPRINT",FACE,{"disambiguationData":[TD([[makeQuery(id+"F12.imprint","IMPRINT",EDGE,{"disambiguationData":[TD([[subQ2,-1.0]])],"derivedFrom":subQ1}),1.0]])]});}
            var Q13;
            {var subQ1=sQuery(id+"F12.wireOp",EDGE,"E77");var subQ4=sQuery(id+"F12.wireOp",EDGE,"E80");var subQ5=makeQuery(id+"F12.imprint","INTERSECT",VERTEX,{"derivedFrom":[subQ1,subQ4]});Q13=makeQuery(id+"F12.imprint","IMPRINT",FACE,{"disambiguationData":[TD([[makeQuery(id+"F12.imprint","IMPRINT",EDGE,{"disambiguationData":[TD([[subQ5,-1.0]])],"derivedFrom":subQ4}),-1.0]])]});}
            var Q14;
            {var subQ1=sQuery(id+"F12.wireOp",EDGE,"E78");var subQ4=sQuery(id+"F12.wireOp",EDGE,"E81");var subQ5=makeQuery(id+"F12.imprint","INTERSECT",VERTEX,{"derivedFrom":[subQ1,subQ4]});Q14=makeQuery(id+"F12.imprint","IMPRINT",FACE,{"disambiguationData":[TD([[makeQuery(id+"F12.imprint","IMPRINT",EDGE,{"disambiguationData":[TD([[subQ5,-1.0]])],"derivedFrom":subQ4}),-1.0]])]});}
            var Q15;
            {var subQ1=sQuery(id+"F12.wireOp",EDGE,"E78");var subQ3=sQuery(id+"F12.wireOp",EDGE,"E81");var subQ4=makeQuery(id+"F12.imprint","INTERSECT",VERTEX,{"derivedFrom":[subQ1,subQ3]});Q15=makeQuery(id+"F12.imprint","IMPRINT",FACE,{"disambiguationData":[TD([[makeQuery(id+"F12.imprint","IMPRINT",EDGE,{"disambiguationData":[TD([[subQ4,1.0]])],"derivedFrom":subQ1}),-1.0]])]});}
            extrude(context, id + "F13", {"entities" : qUnion([Q0, Q1, Q2, Q3, Q4, Q5, Q6, Q7, Q8, Q9, Q10, Q11, Q12, Q13, Q14, Q15]), "oppositeDirection" : true, "depth" : 25 * mm, "offsetDistance" : 25 * mm});
        }
        {
            var Q0;
            Q0=makeQuery(id+"F8.opExtrude","SWEPT_EDGE",EDGE,{"disambiguationData":[OSD([sQuery(id+"F0.wireOp",EDGE,"E14"),sQuery(id+"F0.wireOp",EDGE,"E15")])]});
            var Q1;
            Q1=makeQuery(id+"F8.opExtrude","SWEPT_EDGE",EDGE,{"disambiguationData":[OSD([sQuery(id+"F0.wireOp",EDGE,"E10"),sQuery(id+"F0.wireOp",EDGE,"E11")])]});
            fillet(context, id + "F14", {"entities" : qUnion([Q0, Q1]), "radius" : 1 * mm, "tangentPropagation" : true, "allowEdgeOverflow" : false});
        }
    });
